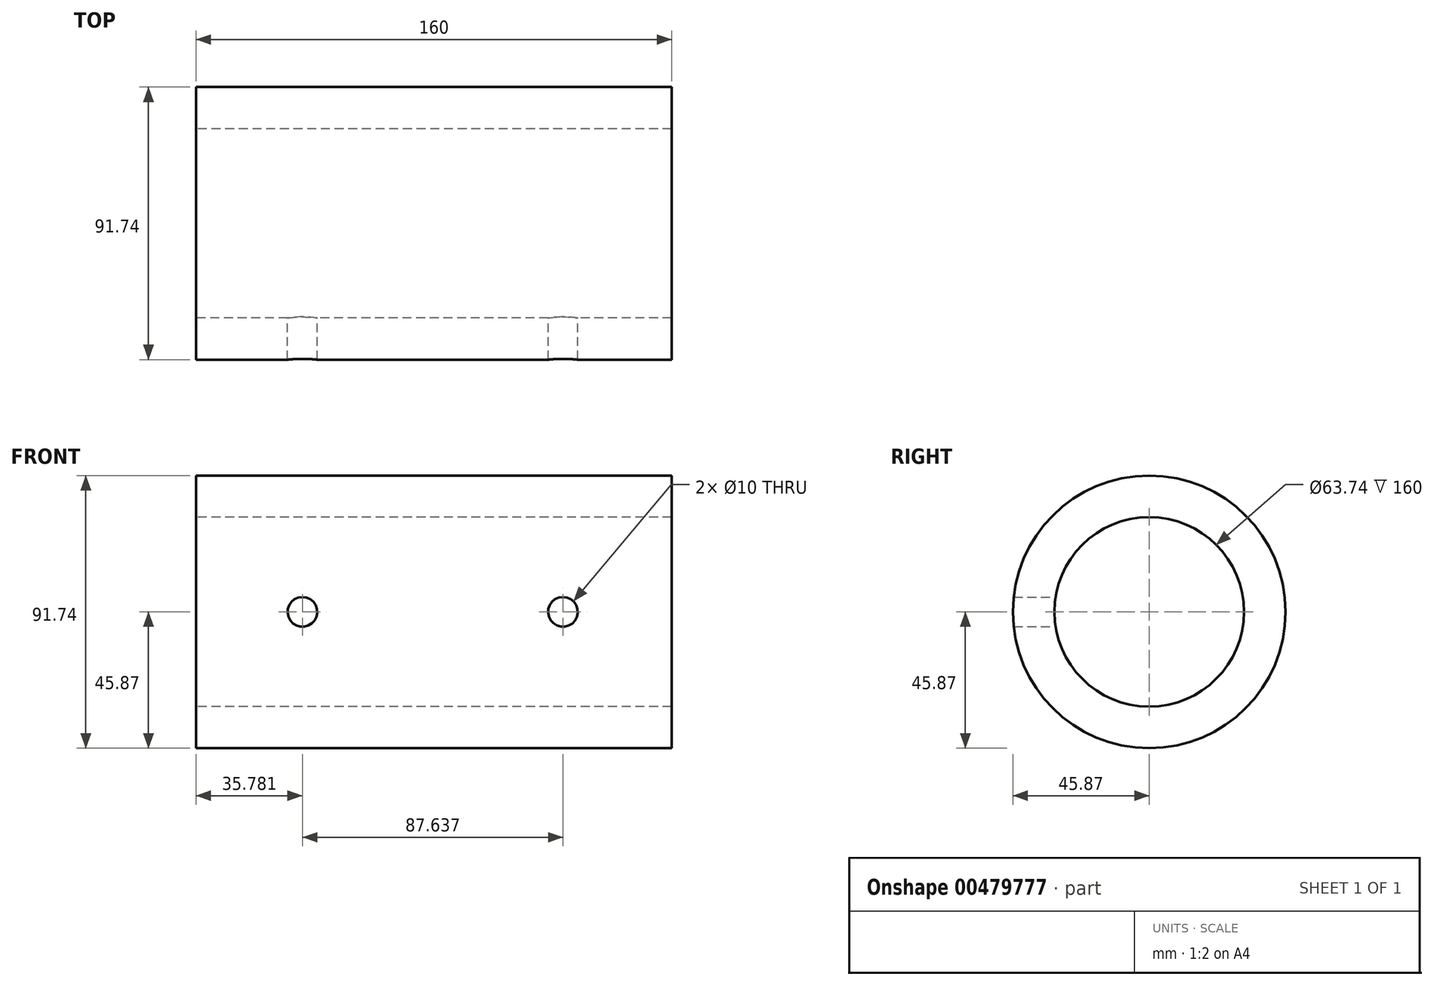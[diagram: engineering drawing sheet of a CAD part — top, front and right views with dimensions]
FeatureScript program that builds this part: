
annotation { "Feature Type Name" : "Feature", "Feature Type Description" : "" }
export const myFeature = defineFeature(function(context is Context, id is Id, definition is map)
    precondition{}
    {
        {
            var Q0;
            Q0=qCreatedBy(makeId("Front.planeOp"),FACE);
            var sketch = newSketch(context, id + "F0", { "sketchPlane" : qUnion([Q0])});
            skLineSegment(sketch, "E0.bottom", {"start": v(-79.6, 45.87) * mm, "end": v(80.4, 45.87) * mm});
            skLineSegment(sketch, "E0.top", {"start": v(-79.6, 31.87) * mm, "end": v(80.4, 31.87) * mm});
            skLineSegment(sketch, "E0.left", {"start": v(-79.6, 45.87) * mm, "end": v(-79.6, 31.87) * mm});
            skLineSegment(sketch, "E0.right", {"start": v(80.4, 45.87) * mm, "end": v(80.4, 31.87) * mm});
            skLineSegment(sketch, "E1", {"start": v(0, 0) * mm, "end": v(119.38, 0) * mm});
            skCircle(sketch, "E2", {"center": v(-1.84, 0) * mm, "radius": 22.42 * mm});
            skSolve(sketch);
        }
        {
            var Q0;
            Q0=makeQuery(id+"F0.imprint","IMPRINT",FACE,{"disambiguationData":[TD([[makeQuery(id+"F0.imprint","IMPRINT",EDGE,{"derivedFrom":sQuery(id+"F0.wireOp",EDGE,"E0.bottom")}),-1.0]])]});
            var Q1;
            Q1=sQuery(id+"F0.wireOp",EDGE,"E1");
            revolve(context, id + "F1", {"entities" : qUnion([Q0]), "axis" : qUnion([Q1]), "revolveType" : RevolveType.FULL});
        }
        {
            var Q0;
            Q0=qCreatedBy(makeId("Front.planeOp"),FACE);
            var sketch = newSketch(context, id + "F2", { "sketchPlane" : qUnion([Q0])});
            skLineSegment(sketch, "E3", {"start": v(-43.82, 42.46) * mm, "end": v(-43.82, -36.52) * mm});
            skCircle(sketch, "E4", {"center": v(-43.82, 0) * mm, "radius": 5 * mm});
            skSolve(sketch);
        }
        {
            var Q0;
            {var subQ0=sQuery(id+"F2.wireOp",EDGE,"E4");var subQ1=sQuery(id+"F2.wireOp",EDGE,"E3");var subQ2=makeQuery(id+"F2.imprint","INTERSECT",VERTEX,{"disambiguationData":[OD(0.0)],"derivedFrom":[subQ1,subQ0]});Q0=makeQuery(id+"F2.imprint","IMPRINT",FACE,{"disambiguationData":[TD([[makeQuery(id+"F2.imprint","IMPRINT",EDGE,{"disambiguationData":[TD([[subQ2,1.0]])],"derivedFrom":subQ1}),1.0]])]});}
            var Q1;
            {var subQ0=sQuery(id+"F2.wireOp",EDGE,"E4");var subQ1=sQuery(id+"F2.wireOp",EDGE,"E3");var subQ2=makeQuery(id+"F2.imprint","INTERSECT",VERTEX,{"disambiguationData":[OD(0.0)],"derivedFrom":[subQ1,subQ0]});Q1=makeQuery(id+"F2.imprint","IMPRINT",FACE,{"disambiguationData":[TD([[makeQuery(id+"F2.imprint","IMPRINT",EDGE,{"disambiguationData":[TD([[subQ2,1.0]])],"derivedFrom":subQ1}),-1.0]])]});}
            extrude(context, id + "F3", {"entities" : qUnion([Q0, Q1]), "operationType" : NewBodyOperationType.REMOVE, "endBound" : BoundingType.THROUGH_ALL, "depth" : 25 * mm});
        }
        {
            var Q0;
            Q0=makeQuery(id+"F3.boolean.opBoolean","COPY",FACE,{"derivedFrom":makeQuery(id+"F3.opExtrude","SWEPT_FACE",FACE,{"disambiguationData":[OSD([sQuery(id+"F2.wireOp",EDGE,"E4")])]})});
            var Q1;
            Q1=qCreatedBy(makeId("Right.planeOp"),FACE);
            mirror(context, id + "F4", {"patternType" : MirrorType.FACE, "faces" : qUnion([Q0]), "mirrorPlane" : qUnion([Q1])});
        }
        {
            var Q0;
            Q0=sQuery(id+"F0.wireOp",EDGE,"E2");
            extrude(context, id + "F5", {"bodyType" : ToolBodyType.SURFACE, "surfaceEntities" : qUnion([Q0]), "endBound" : BoundingType.THROUGH_ALL, "depth" : 25 * mm, "offsetDistance" : 25 * mm});
        }
    });
